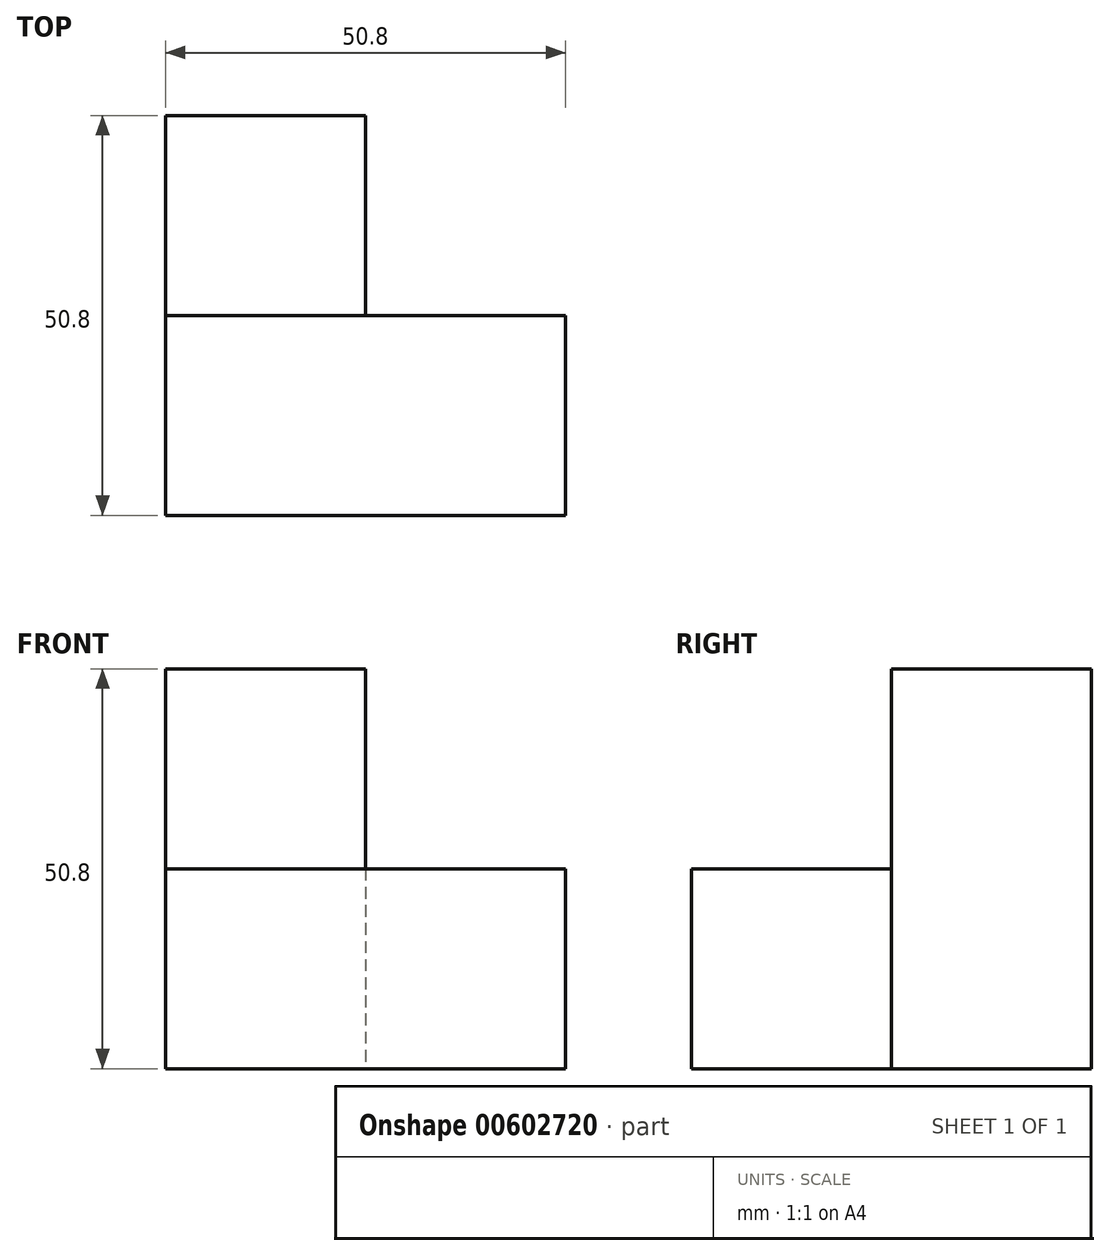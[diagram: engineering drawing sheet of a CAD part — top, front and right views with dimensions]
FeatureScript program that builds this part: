
annotation { "Feature Type Name" : "Feature", "Feature Type Description" : "" }
export const myFeature = defineFeature(function(context is Context, id is Id, definition is map)
    precondition{}
    {
        {
            var Q0;
            Q0=qCreatedBy(makeId("Front.planeOp"),FACE);
            var sketch = newSketch(context, id + "F0", { "sketchPlane" : qUnion([Q0])});
            skLineSegment(sketch, "E0", {"start": v(-46.5, 32.63) * mm, "end": v(-21.1, 32.63) * mm});
            skLineSegment(sketch, "E1", {"start": v(-21.1, 32.63) * mm, "end": v(-21.1, 7.23) * mm});
            skLineSegment(sketch, "E2", {"start": v(-21.1, 7.23) * mm, "end": v(-46.5, 7.23) * mm});
            skLineSegment(sketch, "E3", {"start": v(-46.5, 7.23) * mm, "end": v(-46.5, 32.63) * mm});
            skSolve(sketch);
        }
        {
            var Q0;
            Q0 = qSketchRegion(id + "F0", true);
            extrude(context, id + "F1", {"entities" : qUnion([Q0]), "depth" : 25.4 * mm, "offsetDistance" : 25.4 * mm});
        }
        {
            var Q0;
            Q0=makeQuery(id+"F1.opExtrude","SWEPT_FACE",FACE,{"disambiguationData":[OSD([sQuery(id+"F0.wireOp",EDGE,"E1")])]});
            var sketch = newSketch(context, id + "F2", { "sketchPlane" : qUnion([Q0])});
            skLineSegment(sketch, "E4", {"start": v(-25.4, 32.63) * mm, "end": v(0, 32.63) * mm});
            skLineSegment(sketch, "E5", {"start": v(0, 32.63) * mm, "end": v(0, 7.23) * mm});
            skLineSegment(sketch, "E6", {"start": v(0, 7.23) * mm, "end": v(-25.4, 7.23) * mm});
            skLineSegment(sketch, "E7", {"start": v(-25.4, 7.23) * mm, "end": v(-25.4, 32.63) * mm});
            skSolve(sketch);
        }
        {
            var Q0;
            Q0 = qSketchRegion(id + "F2", true);
            extrude(context, id + "F3", {"entities" : qUnion([Q0]), "operationType" : NewBodyOperationType.ADD, "depth" : 25.4 * mm, "offsetDistance" : 25.4 * mm});
        }
        {
            var Q0;
            Q0=makeQuery(id+"F3.boolean.opBoolean","MERGE",FACE,{"derivedFrom":[makeQuery(id+"F1.opExtrude","CAP_FACE",FACE,{"disambiguationData":[OSD([sQuery(id+"F0.wireOp",EDGE,"E0"),sQuery(id+"F0.wireOp",EDGE,"E1"),sQuery(id+"F0.wireOp",EDGE,"E2"),sQuery(id+"F0.wireOp",EDGE,"E3")])],"isStart":true}),makeQuery(id+"F3.opExtrude","SWEPT_FACE",FACE,{"disambiguationData":[OSD([sQuery(id+"F2.wireOp",EDGE,"E5")])]})]});
            var sketch = newSketch(context, id + "F4", { "sketchPlane" : qUnion([Q0])});
            skLineSegment(sketch, "E8", {"start": v(21.1, 32.63) * mm, "end": v(21.1, 7.23) * mm});
            skLineSegment(sketch, "E9", {"start": v(21.1, 7.23) * mm, "end": v(46.5, 7.23) * mm});
            skLineSegment(sketch, "E10", {"start": v(46.5, 7.23) * mm, "end": v(46.5, 32.63) * mm});
            skLineSegment(sketch, "E11", {"start": v(46.5, 32.63) * mm, "end": v(21.1, 32.63) * mm});
            skSolve(sketch);
        }
        {
            var Q0;
            Q0 = qSketchRegion(id + "F4", true);
            extrude(context, id + "F5", {"entities" : qUnion([Q0]), "operationType" : NewBodyOperationType.ADD, "depth" : 25.4 * mm, "offsetDistance" : 25.4 * mm});
        }
        {
            var Q0;
            Q0=makeQuery(id+"F5.boolean.opBoolean","MERGE",FACE,{"derivedFrom":[makeQuery(id+"F3.boolean.opBoolean","MERGE",FACE,{"derivedFrom":[makeQuery(id+"F1.opExtrude","SWEPT_FACE",FACE,{"disambiguationData":[OSD([sQuery(id+"F0.wireOp",EDGE,"E0")])]}),makeQuery(id+"F3.opExtrude","SWEPT_FACE",FACE,{"disambiguationData":[OSD([sQuery(id+"F2.wireOp",EDGE,"E4")])]})]}),makeQuery(id+"F5.opExtrude","SWEPT_FACE",FACE,{"disambiguationData":[OSD([sQuery(id+"F4.wireOp",EDGE,"E11")])]})]});
            var sketch = newSketch(context, id + "F6", { "sketchPlane" : qUnion([Q0])});
            skLineSegment(sketch, "E12", {"start": v(-46.5, 25.4) * mm, "end": v(-21.1, 25.4) * mm});
            skLineSegment(sketch, "E13", {"start": v(-21.1, 25.4) * mm, "end": v(-21.1, 0) * mm});
            skLineSegment(sketch, "E14", {"start": v(-21.1, 0) * mm, "end": v(-46.5, 0) * mm});
            skLineSegment(sketch, "E15", {"start": v(-46.5, 0) * mm, "end": v(-46.5, 25.4) * mm});
            skSolve(sketch);
        }
        {
            var Q0;
            Q0 = qSketchRegion(id + "F6", true);
            extrude(context, id + "F7", {"entities" : qUnion([Q0]), "operationType" : NewBodyOperationType.ADD, "depth" : 25.4 * mm, "offsetDistance" : 25.4 * mm});
        }
    });
